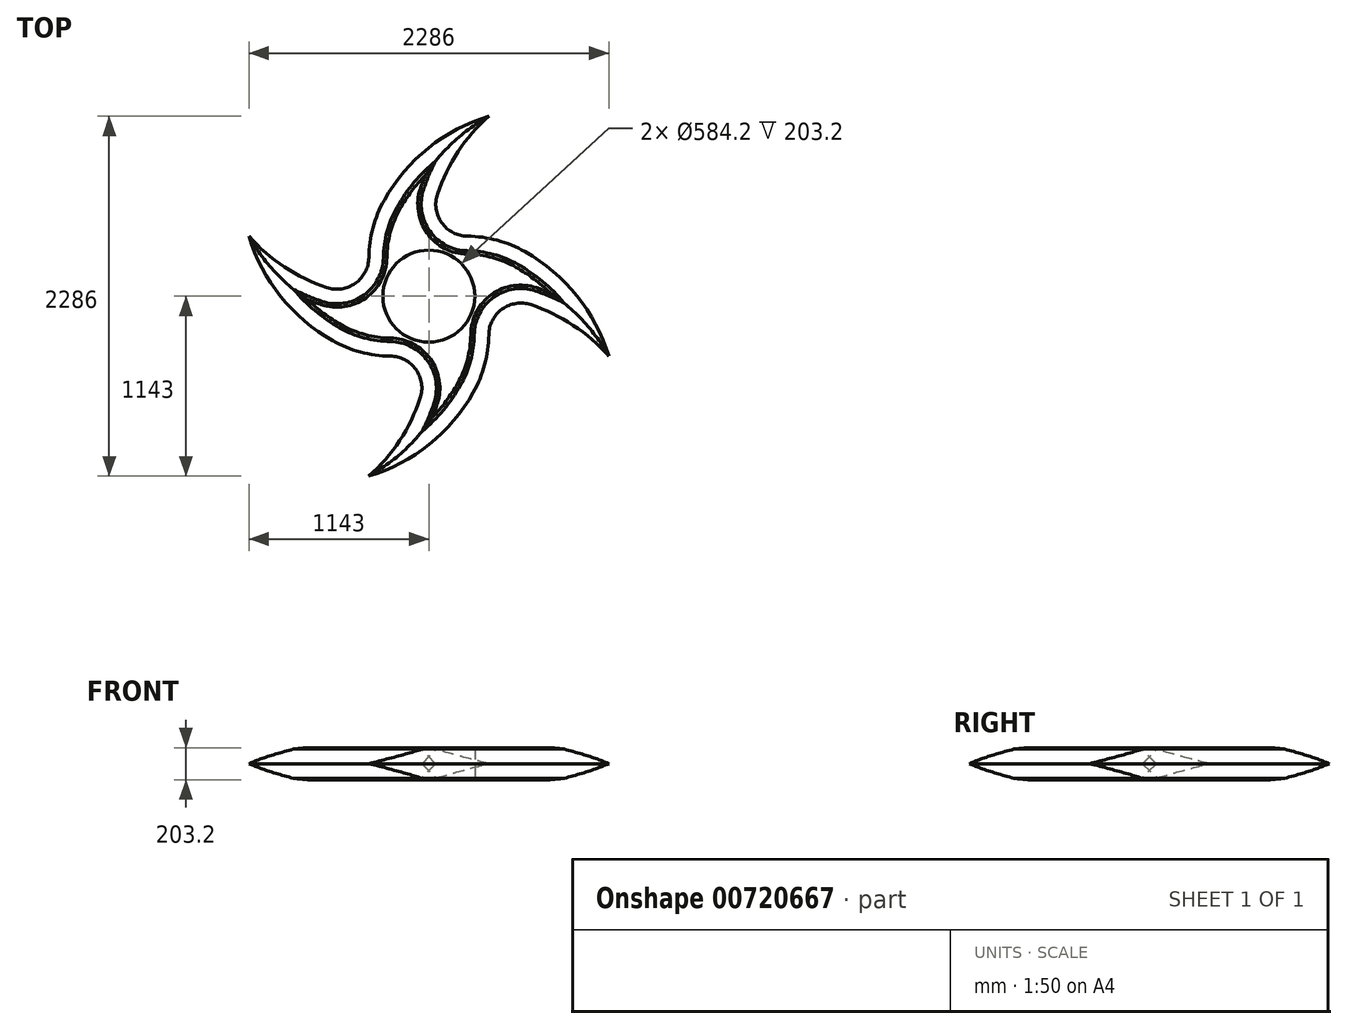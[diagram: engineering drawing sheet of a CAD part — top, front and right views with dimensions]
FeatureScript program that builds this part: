
annotation { "Feature Type Name" : "Feature", "Feature Type Description" : "" }
export const myFeature = defineFeature(function(context is Context, id is Id, definition is map)
    precondition{}
    {
        {
            var Q0;
            Q0=qCreatedBy(makeId("Top.planeOp"),FACE);
            var sketch = newSketch(context, id + "F0", { "sketchPlane" : qUnion([Q0])});
            skCircle(sketch, "E0", {"center": v(0, 0) * mm, "radius": 292.1 * mm});
            skCircle(sketch, "E1", {"center": v(0, 0) * mm, "radius": 381 * mm});
            skLineSegment(sketch, "E2", {"start": v(0, 0) * mm, "end": v(0, 381) * mm});
            skLineSegment(sketch, "E3", {"start": v(0, 381) * mm, "end": v(-381, 381) * mm});
            skLineSegment(sketch, "E4", {"start": v(-381, 381) * mm, "end": v(-381, -381) * mm});
            skLineSegment(sketch, "E5", {"start": v(-381, -381) * mm, "end": v(381, -381) * mm});
            skLineSegment(sketch, "E6", {"start": v(381, -381) * mm, "end": v(381, 381) * mm});
            skLineSegment(sketch, "E7", {"start": v(381, 381) * mm, "end": v(0, 381) * mm});
            skArc(sketch, "E8", {"start": v(381, 1143) * mm, "mid": v(-95.44, 857.44) * mm, "end": v(-381, 381) * mm});
            skArc(sketch, "E9", {"start": v(381, 1143) * mm, "mid": v(116.85, 798.82) * mm, "end": v(0, 381) * mm});
            skArc(sketch, "E10", {"start": v(-1143, 381) * mm, "mid": v(-857.44, -95.44) * mm, "end": v(-381, -381) * mm});
            skArc(sketch, "E11", {"start": v(-1143, 381) * mm, "mid": v(-798.82, 116.85) * mm, "end": v(-381, 0) * mm});
            skArc(sketch, "E12", {"start": v(-381, -1143) * mm, "mid": v(95.44, -857.44) * mm, "end": v(381, -381) * mm});
            skArc(sketch, "E13", {"start": v(-381, -1143) * mm, "mid": v(-116.85, -798.82) * mm, "end": v(0, -381) * mm});
            skArc(sketch, "E14", {"start": v(1143, -381) * mm, "mid": v(857.44, 95.44) * mm, "end": v(381, 381) * mm});
            skArc(sketch, "E15", {"start": v(1143, -381) * mm, "mid": v(798.82, -116.85) * mm, "end": v(381, 0) * mm});
            skSolve(sketch);
        }
        {
            var Q0;
            {var subQ0=sQuery(id+"F0.wireOp",EDGE,"E12");Q0=makeQuery(id+"F0.imprint","IMPRINT",FACE,{"disambiguationData":[TD([[makeQuery(id+"F0.imprint","IMPRINT",EDGE,{"derivedFrom":subQ0}),1.0]])]});}
            var Q1;
            {var subQ0=sQuery(id+"F0.wireOp",EDGE,"E10");Q1=makeQuery(id+"F0.imprint","IMPRINT",FACE,{"disambiguationData":[TD([[makeQuery(id+"F0.imprint","IMPRINT",EDGE,{"derivedFrom":subQ0}),1.0]])]});}
            var Q2;
            Q2=makeQuery(id+"F0.imprint","IMPRINT",FACE,{"disambiguationData":[TD([[makeQuery(id+"F0.imprint","IMPRINT",EDGE,{"derivedFrom":sQuery(id+"F0.wireOp",EDGE,"E3")}),-1.0]])]});
            var Q3;
            {var subQ0=sQuery(id+"F0.wireOp",EDGE,"E14");Q3=makeQuery(id+"F0.imprint","IMPRINT",FACE,{"disambiguationData":[TD([[makeQuery(id+"F0.imprint","IMPRINT",EDGE,{"derivedFrom":subQ0}),1.0]])]});}
            var Q4;
            {var subQ0=sQuery(id+"F0.wireOp",EDGE,"E7");Q4=makeQuery(id+"F0.imprint","IMPRINT",FACE,{"disambiguationData":[TD([[makeQuery(id+"F0.imprint","IMPRINT",EDGE,{"derivedFrom":subQ0}),1.0]])]});}
            var Q5;
            {var subQ0=sQuery(id+"F0.wireOp",EDGE,"E3");Q5=makeQuery(id+"F0.imprint","IMPRINT",FACE,{"disambiguationData":[TD([[makeQuery(id+"F0.imprint","IMPRINT",EDGE,{"derivedFrom":subQ0}),1.0]])]});}
            var Q6;
            Q6=makeQuery(id+"F0.imprint","IMPRINT",FACE,{"disambiguationData":[TD([[makeQuery(id+"F0.imprint","IMPRINT",EDGE,{"derivedFrom":sQuery(id+"F0.wireOp",EDGE,"E0")}),-1.0]])]});
            var Q7;
            {var subQ0=sQuery(id+"F0.wireOp",EDGE,"E4");var subQ1=sQuery(id+"F0.wireOp",EDGE,"E1");var subQ2=makeQuery(id+"F0.imprint","INTERSECT",VERTEX,{"derivedFrom":[subQ1,subQ0,sQuery(id+"F0.wireOp",EDGE,"E11")]});Q7=makeQuery(id+"F0.imprint","IMPRINT",FACE,{"disambiguationData":[TD([[makeQuery(id+"F0.imprint","IMPRINT",EDGE,{"disambiguationData":[TD([[subQ2,-1.0]])],"derivedFrom":subQ1}),-1.0]])]});}
            var Q8;
            {var subQ0=sQuery(id+"F0.wireOp",EDGE,"E5");var subQ1=sQuery(id+"F0.wireOp",EDGE,"E1");var subQ2=makeQuery(id+"F0.imprint","INTERSECT",VERTEX,{"derivedFrom":[subQ1,subQ0,sQuery(id+"F0.wireOp",EDGE,"E13")]});Q8=makeQuery(id+"F0.imprint","IMPRINT",FACE,{"disambiguationData":[TD([[makeQuery(id+"F0.imprint","IMPRINT",EDGE,{"disambiguationData":[TD([[subQ2,-1.0]])],"derivedFrom":subQ1}),-1.0]])]});}
            extrude(context, id + "F1", {"entities" : qUnion([Q0, Q1, Q2, Q3, Q4, Q5, Q6, Q7, Q8]), "depth" : 203.2 * mm, "offsetDistance" : 25.4 * mm});
        }
        {
            var Q0;
            Q0=makeQuery(id+"F1.opExtrude","SWEPT_EDGE",EDGE,{"disambiguationData":[OSD([sQuery(id+"F0.wireOp",EDGE,"E6"),sQuery(id+"F0.wireOp",EDGE,"E7"),sQuery(id+"F0.wireOp",EDGE,"E14")])]});
            var Q1;
            Q1=makeQuery(id+"F1.opExtrude","SWEPT_EDGE",EDGE,{"disambiguationData":[OSD([sQuery(id+"F0.wireOp",EDGE,"E3"),sQuery(id+"F0.wireOp",EDGE,"E4"),sQuery(id+"F0.wireOp",EDGE,"E8")])]});
            var Q2;
            Q2=makeQuery(id+"F1.opExtrude","SWEPT_EDGE",EDGE,{"disambiguationData":[OSD([sQuery(id+"F0.wireOp",EDGE,"E4"),sQuery(id+"F0.wireOp",EDGE,"E5"),sQuery(id+"F0.wireOp",EDGE,"E10")])]});
            var Q3;
            Q3=makeQuery(id+"F1.opExtrude","SWEPT_EDGE",EDGE,{"disambiguationData":[OSD([sQuery(id+"F0.wireOp",EDGE,"E5"),sQuery(id+"F0.wireOp",EDGE,"E6"),sQuery(id+"F0.wireOp",EDGE,"E12")])]});
            fillet(context, id + "F2", {"entities" : qUnion([Q0, Q1, Q2, Q3]), "radius" : 762 * mm, "tangentPropagation" : true, "allowEdgeOverflow" : false});
        }
        {
            var Q0;
            Q0=makeQuery(id+"F1.opExtrude","SWEPT_EDGE",EDGE,{"disambiguationData":[OSD([sQuery(id+"F0.wireOp",EDGE,"E1"),sQuery(id+"F0.wireOp",EDGE,"E4"),sQuery(id+"F0.wireOp",EDGE,"E11")])]});
            var Q1;
            Q1=makeQuery(id+"F1.opExtrude","SWEPT_EDGE",EDGE,{"disambiguationData":[OSD([sQuery(id+"F0.wireOp",EDGE,"E1"),sQuery(id+"F0.wireOp",EDGE,"E5"),sQuery(id+"F0.wireOp",EDGE,"E13")])]});
            var Q2;
            Q2=makeQuery(id+"F1.opExtrude","SWEPT_EDGE",EDGE,{"disambiguationData":[OSD([sQuery(id+"F0.wireOp",EDGE,"E1"),sQuery(id+"F0.wireOp",EDGE,"E6"),sQuery(id+"F0.wireOp",EDGE,"E15")])]});
            var Q3;
            Q3=makeQuery(id+"F1.opExtrude","SWEPT_EDGE",EDGE,{"disambiguationData":[OSD([sQuery(id+"F0.wireOp",EDGE,"E1"),sQuery(id+"F0.wireOp",EDGE,"E3"),sQuery(id+"F0.wireOp",EDGE,"E7"),sQuery(id+"F0.wireOp",EDGE,"E9")])]});
            fillet(context, id + "F3", {"entities" : qUnion([Q0, Q1, Q2, Q3]), "radius" : 203.2 * mm, "tangentPropagation" : true, "allowEdgeOverflow" : false});
        }
        {
            var Q0;
            Q0=makeQuery(id+"F1.opExtrude","CAP_EDGE",EDGE,{"disambiguationData":[OSD([sQuery(id+"F0.wireOp",EDGE,"E9")])],"isStart":false});
            var Q1;
            Q1=makeQuery(id+"F1.opExtrude","CAP_EDGE",EDGE,{"disambiguationData":[OSD([sQuery(id+"F0.wireOp",EDGE,"E9")])],"isStart":true});
            var Q2;
            Q2=makeQuery(id+"F1.opExtrude","CAP_EDGE",EDGE,{"disambiguationData":[OSD([sQuery(id+"F0.wireOp",EDGE,"E13")])],"isStart":true});
            var Q3;
            Q3=makeQuery(id+"F1.opExtrude","CAP_EDGE",EDGE,{"disambiguationData":[OSD([sQuery(id+"F0.wireOp",EDGE,"E13")])],"isStart":false});
            var Q4;
            Q4=makeQuery(id+"F1.opExtrude","CAP_EDGE",EDGE,{"disambiguationData":[OSD([sQuery(id+"F0.wireOp",EDGE,"E11")])],"isStart":false});
            var Q5;
            Q5=makeQuery(id+"F1.opExtrude","CAP_EDGE",EDGE,{"disambiguationData":[OSD([sQuery(id+"F0.wireOp",EDGE,"E11")])],"isStart":true});
            var Q6;
            {var subQ0=sQuery(id+"F0.wireOp",EDGE,"E15");var subQ1=sQuery(id+"F0.wireOp",EDGE,"E6");Q6=makeQuery(id+"F3.opFillet","BLEND_EDGE",EDGE,{"blendedFrom":[makeQuery(id+"F1.opExtrude","SWEPT_EDGE",EDGE,{"disambiguationData":[OSD([sQuery(id+"F0.wireOp",EDGE,"E1"),subQ1,subQ0])]}),makeQuery(id+"F1.opExtrude","CAP_FACE",FACE,{"disambiguationData":[OSD([sQuery(id+"F0.wireOp",EDGE,"E0"),sQuery(id+"F0.wireOp",EDGE,"E4"),sQuery(id+"F0.wireOp",EDGE,"E5"),subQ1,sQuery(id+"F0.wireOp",EDGE,"E7"),sQuery(id+"F0.wireOp",EDGE,"E8"),sQuery(id+"F0.wireOp",EDGE,"E9"),sQuery(id+"F0.wireOp",EDGE,"E10"),sQuery(id+"F0.wireOp",EDGE,"E11"),sQuery(id+"F0.wireOp",EDGE,"E12"),sQuery(id+"F0.wireOp",EDGE,"E13"),sQuery(id+"F0.wireOp",EDGE,"E14"),subQ0])],"isStart":false})],"blendedInto":[makeQuery(id+"F1.opExtrude","CAP_FACE",FACE,{"disambiguationData":[OSD([sQuery(id+"F0.wireOp",EDGE,"E0"),sQuery(id+"F0.wireOp",EDGE,"E4"),sQuery(id+"F0.wireOp",EDGE,"E5"),subQ1,sQuery(id+"F0.wireOp",EDGE,"E7"),sQuery(id+"F0.wireOp",EDGE,"E8"),sQuery(id+"F0.wireOp",EDGE,"E9"),sQuery(id+"F0.wireOp",EDGE,"E10"),sQuery(id+"F0.wireOp",EDGE,"E11"),sQuery(id+"F0.wireOp",EDGE,"E12"),sQuery(id+"F0.wireOp",EDGE,"E13"),sQuery(id+"F0.wireOp",EDGE,"E14"),subQ0])],"isStart":false})]});}
            var Q7;
            {var subQ0=sQuery(id+"F0.wireOp",EDGE,"E15");var subQ1=sQuery(id+"F0.wireOp",EDGE,"E6");Q7=makeQuery(id+"F3.opFillet","BLEND_EDGE",EDGE,{"blendedFrom":[makeQuery(id+"F1.opExtrude","SWEPT_EDGE",EDGE,{"disambiguationData":[OSD([sQuery(id+"F0.wireOp",EDGE,"E1"),subQ1,subQ0])]}),makeQuery(id+"F1.opExtrude","CAP_FACE",FACE,{"disambiguationData":[OSD([sQuery(id+"F0.wireOp",EDGE,"E0"),sQuery(id+"F0.wireOp",EDGE,"E4"),sQuery(id+"F0.wireOp",EDGE,"E5"),subQ1,sQuery(id+"F0.wireOp",EDGE,"E7"),sQuery(id+"F0.wireOp",EDGE,"E8"),sQuery(id+"F0.wireOp",EDGE,"E9"),sQuery(id+"F0.wireOp",EDGE,"E10"),sQuery(id+"F0.wireOp",EDGE,"E11"),sQuery(id+"F0.wireOp",EDGE,"E12"),sQuery(id+"F0.wireOp",EDGE,"E13"),sQuery(id+"F0.wireOp",EDGE,"E14"),subQ0])],"isStart":true})],"blendedInto":[makeQuery(id+"F1.opExtrude","CAP_FACE",FACE,{"disambiguationData":[OSD([sQuery(id+"F0.wireOp",EDGE,"E0"),sQuery(id+"F0.wireOp",EDGE,"E4"),sQuery(id+"F0.wireOp",EDGE,"E5"),subQ1,sQuery(id+"F0.wireOp",EDGE,"E7"),sQuery(id+"F0.wireOp",EDGE,"E8"),sQuery(id+"F0.wireOp",EDGE,"E9"),sQuery(id+"F0.wireOp",EDGE,"E10"),sQuery(id+"F0.wireOp",EDGE,"E11"),sQuery(id+"F0.wireOp",EDGE,"E12"),sQuery(id+"F0.wireOp",EDGE,"E13"),sQuery(id+"F0.wireOp",EDGE,"E14"),subQ0])],"isStart":true})]});}
            chamfer(context, id + "F4", {"entities" : qUnion([Q0, Q1, Q2, Q3, Q4, Q5, Q6, Q7]), "width" : 101.6 * mm, "tangentPropagation" : true});
        }
        {
            var Q0;
            {var subQ0=sQuery(id+"F0.wireOp",EDGE,"E15");var subQ1=sQuery(id+"F0.wireOp",EDGE,"E6");var subQ2=makeQuery(id+"F1.opExtrude","CAP_FACE",FACE,{"disambiguationData":[OSD([sQuery(id+"F0.wireOp",EDGE,"E0"),sQuery(id+"F0.wireOp",EDGE,"E4"),sQuery(id+"F0.wireOp",EDGE,"E5"),subQ1,sQuery(id+"F0.wireOp",EDGE,"E7"),sQuery(id+"F0.wireOp",EDGE,"E8"),sQuery(id+"F0.wireOp",EDGE,"E9"),sQuery(id+"F0.wireOp",EDGE,"E10"),sQuery(id+"F0.wireOp",EDGE,"E11"),sQuery(id+"F0.wireOp",EDGE,"E12"),sQuery(id+"F0.wireOp",EDGE,"E13"),sQuery(id+"F0.wireOp",EDGE,"E14"),subQ0])],"isStart":false});Q0=makeQuery(id+"F4.opChamfer","BLEND_EDGE",EDGE,{"blendedFrom":[makeQuery(id+"F3.opFillet","BLEND_EDGE",EDGE,{"blendedFrom":[makeQuery(id+"F1.opExtrude","SWEPT_EDGE",EDGE,{"disambiguationData":[OSD([sQuery(id+"F0.wireOp",EDGE,"E1"),subQ1,subQ0])]}),subQ2],"blendedInto":[subQ2]}),subQ2],"blendedInto":[subQ2]});}
            var Q1;
            {var subQ0=sQuery(id+"F0.wireOp",EDGE,"E14");var subQ1=sQuery(id+"F0.wireOp",EDGE,"E7");var subQ2=sQuery(id+"F0.wireOp",EDGE,"E6");var subQ3=makeQuery(id+"F1.opExtrude","CAP_FACE",FACE,{"disambiguationData":[OSD([sQuery(id+"F0.wireOp",EDGE,"E0"),sQuery(id+"F0.wireOp",EDGE,"E4"),sQuery(id+"F0.wireOp",EDGE,"E5"),subQ2,subQ1,sQuery(id+"F0.wireOp",EDGE,"E8"),sQuery(id+"F0.wireOp",EDGE,"E9"),sQuery(id+"F0.wireOp",EDGE,"E10"),sQuery(id+"F0.wireOp",EDGE,"E11"),sQuery(id+"F0.wireOp",EDGE,"E12"),sQuery(id+"F0.wireOp",EDGE,"E13"),subQ0,sQuery(id+"F0.wireOp",EDGE,"E15")])],"isStart":false});Q1=makeQuery(id+"F4.opChamfer","BLEND_EDGE",EDGE,{"blendedFrom":[makeQuery(id+"F2.opFillet","BLEND_EDGE",EDGE,{"blendedFrom":[makeQuery(id+"F1.opExtrude","SWEPT_EDGE",EDGE,{"disambiguationData":[OSD([subQ2,subQ1,subQ0])]}),subQ3],"blendedInto":[subQ3]}),subQ3],"blendedInto":[subQ3]});}
            var Q2;
            {var subQ0=sQuery(id+"F0.wireOp",EDGE,"E13");var subQ1=sQuery(id+"F0.wireOp",EDGE,"E5");var subQ2=makeQuery(id+"F1.opExtrude","CAP_FACE",FACE,{"disambiguationData":[OSD([sQuery(id+"F0.wireOp",EDGE,"E0"),sQuery(id+"F0.wireOp",EDGE,"E4"),subQ1,sQuery(id+"F0.wireOp",EDGE,"E6"),sQuery(id+"F0.wireOp",EDGE,"E7"),sQuery(id+"F0.wireOp",EDGE,"E8"),sQuery(id+"F0.wireOp",EDGE,"E9"),sQuery(id+"F0.wireOp",EDGE,"E10"),sQuery(id+"F0.wireOp",EDGE,"E11"),sQuery(id+"F0.wireOp",EDGE,"E12"),subQ0,sQuery(id+"F0.wireOp",EDGE,"E14"),sQuery(id+"F0.wireOp",EDGE,"E15")])],"isStart":false});Q2=makeQuery(id+"F4.opChamfer","BLEND_EDGE",EDGE,{"blendedFrom":[makeQuery(id+"F3.opFillet","BLEND_EDGE",EDGE,{"blendedFrom":[makeQuery(id+"F1.opExtrude","SWEPT_EDGE",EDGE,{"disambiguationData":[OSD([sQuery(id+"F0.wireOp",EDGE,"E1"),subQ1,subQ0])]}),subQ2],"blendedInto":[subQ2]}),subQ2],"blendedInto":[subQ2]});}
            var Q3;
            {var subQ0=sQuery(id+"F0.wireOp",EDGE,"E11");var subQ1=sQuery(id+"F0.wireOp",EDGE,"E4");var subQ2=makeQuery(id+"F1.opExtrude","CAP_FACE",FACE,{"disambiguationData":[OSD([sQuery(id+"F0.wireOp",EDGE,"E0"),subQ1,sQuery(id+"F0.wireOp",EDGE,"E5"),sQuery(id+"F0.wireOp",EDGE,"E6"),sQuery(id+"F0.wireOp",EDGE,"E7"),sQuery(id+"F0.wireOp",EDGE,"E8"),sQuery(id+"F0.wireOp",EDGE,"E9"),sQuery(id+"F0.wireOp",EDGE,"E10"),subQ0,sQuery(id+"F0.wireOp",EDGE,"E12"),sQuery(id+"F0.wireOp",EDGE,"E13"),sQuery(id+"F0.wireOp",EDGE,"E14"),sQuery(id+"F0.wireOp",EDGE,"E15")])],"isStart":false});Q3=makeQuery(id+"F4.opChamfer","BLEND_EDGE",EDGE,{"blendedFrom":[makeQuery(id+"F3.opFillet","BLEND_EDGE",EDGE,{"blendedFrom":[makeQuery(id+"F1.opExtrude","SWEPT_EDGE",EDGE,{"disambiguationData":[OSD([sQuery(id+"F0.wireOp",EDGE,"E1"),subQ1,subQ0])]}),subQ2],"blendedInto":[subQ2]}),subQ2],"blendedInto":[subQ2]});}
            var Q4;
            {var subQ0=sQuery(id+"F0.wireOp",EDGE,"E11");var subQ1=sQuery(id+"F0.wireOp",EDGE,"E4");var subQ2=makeQuery(id+"F1.opExtrude","CAP_FACE",FACE,{"disambiguationData":[OSD([sQuery(id+"F0.wireOp",EDGE,"E0"),subQ1,sQuery(id+"F0.wireOp",EDGE,"E5"),sQuery(id+"F0.wireOp",EDGE,"E6"),sQuery(id+"F0.wireOp",EDGE,"E7"),sQuery(id+"F0.wireOp",EDGE,"E8"),sQuery(id+"F0.wireOp",EDGE,"E9"),sQuery(id+"F0.wireOp",EDGE,"E10"),subQ0,sQuery(id+"F0.wireOp",EDGE,"E12"),sQuery(id+"F0.wireOp",EDGE,"E13"),sQuery(id+"F0.wireOp",EDGE,"E14"),sQuery(id+"F0.wireOp",EDGE,"E15")])],"isStart":true});Q4=makeQuery(id+"F4.opChamfer","BLEND_EDGE",EDGE,{"blendedFrom":[makeQuery(id+"F3.opFillet","BLEND_EDGE",EDGE,{"blendedFrom":[makeQuery(id+"F1.opExtrude","SWEPT_EDGE",EDGE,{"disambiguationData":[OSD([sQuery(id+"F0.wireOp",EDGE,"E1"),subQ1,subQ0])]}),subQ2],"blendedInto":[subQ2]}),subQ2],"blendedInto":[subQ2]});}
            var Q5;
            {var subQ0=sQuery(id+"F0.wireOp",EDGE,"E10");var subQ1=sQuery(id+"F0.wireOp",EDGE,"E5");var subQ2=sQuery(id+"F0.wireOp",EDGE,"E4");var subQ3=makeQuery(id+"F1.opExtrude","CAP_FACE",FACE,{"disambiguationData":[OSD([sQuery(id+"F0.wireOp",EDGE,"E0"),subQ2,subQ1,sQuery(id+"F0.wireOp",EDGE,"E6"),sQuery(id+"F0.wireOp",EDGE,"E7"),sQuery(id+"F0.wireOp",EDGE,"E8"),sQuery(id+"F0.wireOp",EDGE,"E9"),subQ0,sQuery(id+"F0.wireOp",EDGE,"E11"),sQuery(id+"F0.wireOp",EDGE,"E12"),sQuery(id+"F0.wireOp",EDGE,"E13"),sQuery(id+"F0.wireOp",EDGE,"E14"),sQuery(id+"F0.wireOp",EDGE,"E15")])],"isStart":true});Q5=makeQuery(id+"F4.opChamfer","BLEND_EDGE",EDGE,{"blendedFrom":[makeQuery(id+"F2.opFillet","BLEND_EDGE",EDGE,{"blendedFrom":[makeQuery(id+"F1.opExtrude","SWEPT_EDGE",EDGE,{"disambiguationData":[OSD([subQ2,subQ1,subQ0])]}),subQ3],"blendedInto":[subQ3]}),subQ3],"blendedInto":[subQ3]});}
            var Q6;
            {var subQ0=sQuery(id+"F0.wireOp",EDGE,"E12");var subQ1=sQuery(id+"F0.wireOp",EDGE,"E6");var subQ2=sQuery(id+"F0.wireOp",EDGE,"E5");var subQ3=makeQuery(id+"F1.opExtrude","CAP_FACE",FACE,{"disambiguationData":[OSD([sQuery(id+"F0.wireOp",EDGE,"E0"),sQuery(id+"F0.wireOp",EDGE,"E4"),subQ2,subQ1,sQuery(id+"F0.wireOp",EDGE,"E7"),sQuery(id+"F0.wireOp",EDGE,"E8"),sQuery(id+"F0.wireOp",EDGE,"E9"),sQuery(id+"F0.wireOp",EDGE,"E10"),sQuery(id+"F0.wireOp",EDGE,"E11"),subQ0,sQuery(id+"F0.wireOp",EDGE,"E13"),sQuery(id+"F0.wireOp",EDGE,"E14"),sQuery(id+"F0.wireOp",EDGE,"E15")])],"isStart":true});Q6=makeQuery(id+"F4.opChamfer","BLEND_EDGE",EDGE,{"blendedFrom":[makeQuery(id+"F2.opFillet","BLEND_EDGE",EDGE,{"blendedFrom":[makeQuery(id+"F1.opExtrude","SWEPT_EDGE",EDGE,{"disambiguationData":[OSD([subQ2,subQ1,subQ0])]}),subQ3],"blendedInto":[subQ3]}),subQ3],"blendedInto":[subQ3]});}
            var Q7;
            {var subQ0=sQuery(id+"F0.wireOp",EDGE,"E9");var subQ1=sQuery(id+"F0.wireOp",EDGE,"E7");var subQ2=makeQuery(id+"F1.opExtrude","CAP_FACE",FACE,{"disambiguationData":[OSD([sQuery(id+"F0.wireOp",EDGE,"E0"),sQuery(id+"F0.wireOp",EDGE,"E4"),sQuery(id+"F0.wireOp",EDGE,"E5"),sQuery(id+"F0.wireOp",EDGE,"E6"),subQ1,sQuery(id+"F0.wireOp",EDGE,"E8"),subQ0,sQuery(id+"F0.wireOp",EDGE,"E10"),sQuery(id+"F0.wireOp",EDGE,"E11"),sQuery(id+"F0.wireOp",EDGE,"E12"),sQuery(id+"F0.wireOp",EDGE,"E13"),sQuery(id+"F0.wireOp",EDGE,"E14"),sQuery(id+"F0.wireOp",EDGE,"E15")])],"isStart":true});Q7=makeQuery(id+"F4.opChamfer","BLEND_EDGE",EDGE,{"blendedFrom":[makeQuery(id+"F3.opFillet","BLEND_EDGE",EDGE,{"blendedFrom":[makeQuery(id+"F1.opExtrude","SWEPT_EDGE",EDGE,{"disambiguationData":[OSD([sQuery(id+"F0.wireOp",EDGE,"E1"),sQuery(id+"F0.wireOp",EDGE,"E3"),subQ1,subQ0])]}),subQ2],"blendedInto":[subQ2]}),subQ2],"blendedInto":[subQ2]});}
            chamfer(context, id + "F5", {"entities" : qUnion([Q0, Q1, Q2, Q3, Q4, Q5, Q6, Q7]), "width" : 30.48 * mm, "tangentPropagation" : true});
        }
    });
